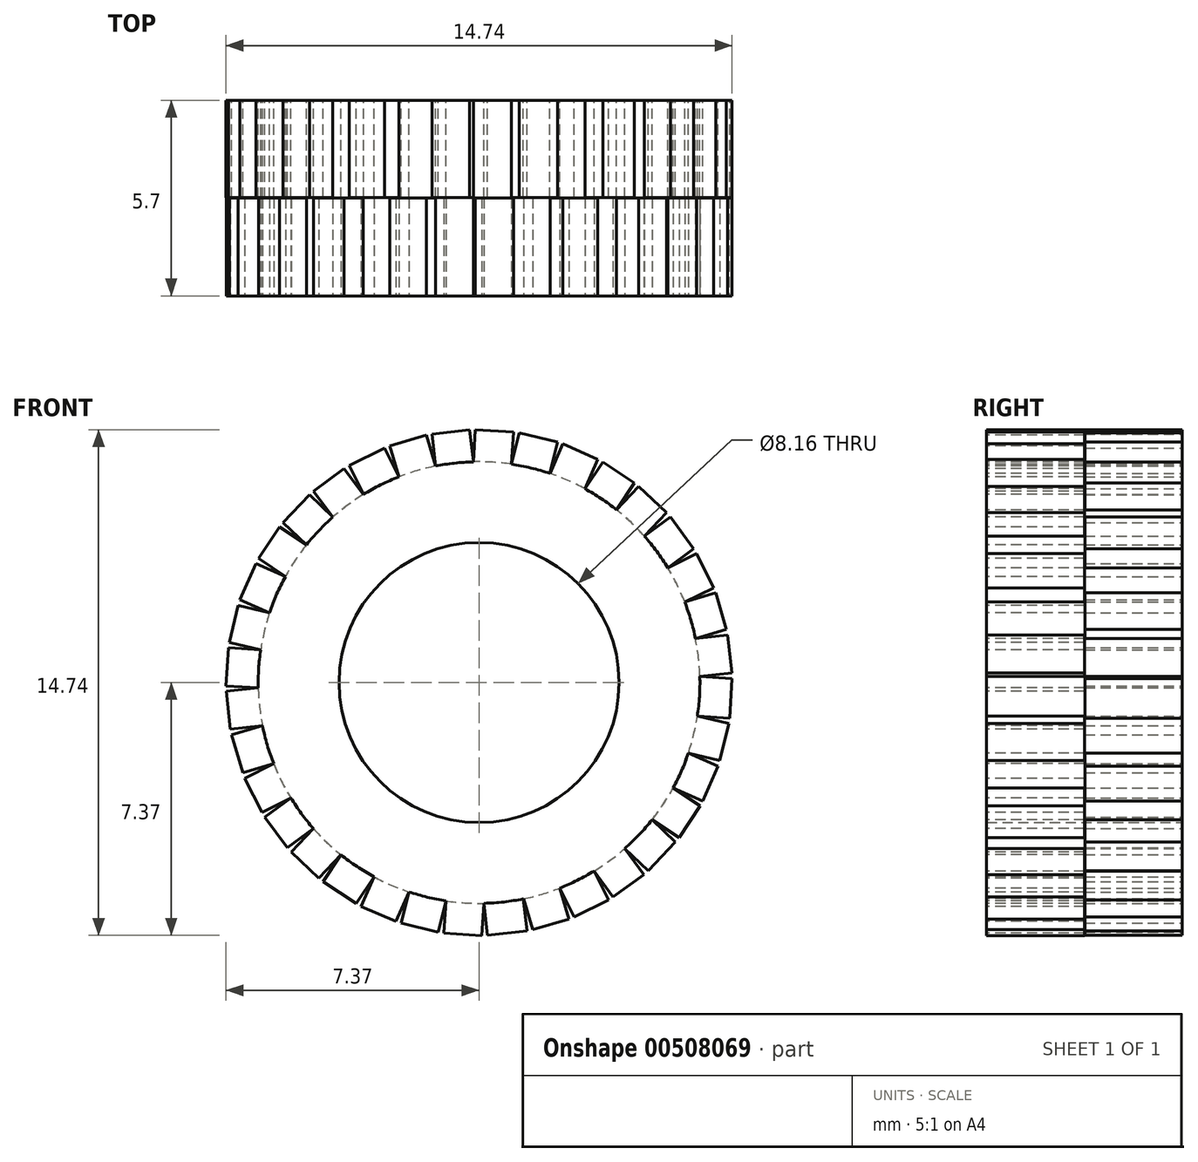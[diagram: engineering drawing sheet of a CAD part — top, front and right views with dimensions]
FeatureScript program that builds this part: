
annotation { "Feature Type Name" : "Feature", "Feature Type Description" : "" }
export const myFeature = defineFeature(function(context is Context, id is Id, definition is map)
    precondition{}
    {
        {
            var Q0;
            Q0=qCreatedBy(makeId("Front.planeOp"),FACE);
            var sketch = newSketch(context, id + "F0", { "sketchPlane" : qUnion([Q0])});
            skCircle(sketch, "E0", {"center": v(0, 0) * mm, "radius": 6.44 * mm});
            skCircle(sketch, "E1", {"center": v(0, 0) * mm, "radius": 4.08 * mm});
            skSolve(sketch);
        }
        {
            var Q0;
            Q0 = qSketchRegion(id + "F0", true);
            extrude(context, id + "F1", {"entities" : qUnion([Q0]), "depth" : 5.7 * mm, "offsetDistance" : 25 * mm});
        }
        {
            var Q0;
            Q0=makeQuery(id+"F1.opExtrude","CAP_FACE",FACE,{"disambiguationData":[OSD([sQuery(id+"F0.wireOp",EDGE,"E0"),sQuery(id+"F0.wireOp",EDGE,"E1")])],"isStart":false});
            var sketch = newSketch(context, id + "F2", { "sketchPlane" : qUnion([Q0])});
            skLineSegment(sketch, "E2", {"start": v(-2.33, 6) * mm, "end": v(-1.27, 6.3) * mm});
            skPoint(sketch, "E3.startSnap0", {"position": v(-1.8, 6.15) * mm});
            skLineSegment(sketch, "E4", {"start": v(-1.27, 6.3) * mm, "end": v(-1.53, 7.21) * mm});
            skLineSegment(sketch, "E5", {"start": v(-2.33, 6) * mm, "end": v(-2.6, 6.9) * mm});
            skLineSegment(sketch, "E6", {"start": v(-2.6, 6.9) * mm, "end": v(-1.53, 7.21) * mm});
            skLineSegment(sketch, "E7", {"start": v(-1.27, 6.3) * mm, "end": v(-0.17, 6.43) * mm});
            skLineSegment(sketch, "E8", {"start": v(-0.17, 6.43) * mm, "end": v(-0.1, 7.37) * mm});
            skLineSegment(sketch, "E9", {"start": v(-0.17, 6.43) * mm, "end": v(0.94, 6.37) * mm});
            skLineSegment(sketch, "E10", {"start": v(0.94, 6.37) * mm, "end": v(1, 7.3) * mm});
            skLineSegment(sketch, "E11", {"start": v(-0.1, 7.37) * mm, "end": v(1, 7.3) * mm});
            skLineSegment(sketch, "E12.1.0", {"start": v(-4.26, 4.82) * mm, "end": v(-4.82, 5.58) * mm});
            skLineSegment(sketch, "E12.1.1", {"start": v(-4.82, 5.58) * mm, "end": v(-3.93, 6.24) * mm});
            skLineSegment(sketch, "E12.1.2", {"start": v(-4.26, 4.82) * mm, "end": v(-3.37, 5.48) * mm});
            skLineSegment(sketch, "E12.1.3", {"start": v(-3.37, 5.48) * mm, "end": v(-3.93, 6.24) * mm});
            skLineSegment(sketch, "E12.1.4", {"start": v(-5.03, 4.02) * mm, "end": v(-4.26, 4.82) * mm});
            skLineSegment(sketch, "E12.1.5", {"start": v(-5.64, 3.1) * mm, "end": v(-5.03, 4.02) * mm});
            skLineSegment(sketch, "E12.1.6", {"start": v(-5.03, 4.02) * mm, "end": v(-5.8, 4.54) * mm});
            skLineSegment(sketch, "E12.1.7", {"start": v(-6.42, 3.61) * mm, "end": v(-5.8, 4.54) * mm});
            skLineSegment(sketch, "E12.1.8", {"start": v(-5.64, 3.1) * mm, "end": v(-6.42, 3.61) * mm});
            skLineSegment(sketch, "E12.2.0", {"start": v(-6.36, 0.95) * mm, "end": v(-7.28, 1.17) * mm});
            skLineSegment(sketch, "E12.2.1", {"start": v(-7.28, 1.17) * mm, "end": v(-7.02, 2.25) * mm});
            skLineSegment(sketch, "E12.2.2", {"start": v(-6.36, 0.95) * mm, "end": v(-6.1, 2.03) * mm});
            skLineSegment(sketch, "E12.2.3", {"start": v(-6.1, 2.03) * mm, "end": v(-7.02, 2.25) * mm});
            skLineSegment(sketch, "E12.2.4", {"start": v(-6.43, -0.15) * mm, "end": v(-6.36, 0.95) * mm});
            skLineSegment(sketch, "E12.2.5", {"start": v(-6.31, -1.26) * mm, "end": v(-6.43, -0.15) * mm});
            skLineSegment(sketch, "E12.2.6", {"start": v(-6.43, -0.15) * mm, "end": v(-7.37, -0.26) * mm});
            skLineSegment(sketch, "E12.2.7", {"start": v(-7.25, -1.36) * mm, "end": v(-7.37, -0.26) * mm});
            skLineSegment(sketch, "E12.2.8", {"start": v(-6.31, -1.26) * mm, "end": v(-7.25, -1.36) * mm});
            skPoint(sketch, "E12.center", {"position": v(0, 0) * mm});
            skLineSegment(sketch, "E13.1.3.0", {"start": v(-5.49, -3.36) * mm, "end": v(-6.33, -3.78) * mm});
            skLineSegment(sketch, "E13.3.3.0", {"start": v(-6.33, -3.78) * mm, "end": v(-6.82, -2.79) * mm});
            skLineSegment(sketch, "E13.6.3.0", {"start": v(-5.49, -3.36) * mm, "end": v(-5.98, -2.37) * mm});
            skLineSegment(sketch, "E13.9.3.0", {"start": v(-5.98, -2.37) * mm, "end": v(-6.82, -2.79) * mm});
            skLineSegment(sketch, "E13.12.3.0", {"start": v(-4.83, -4.25) * mm, "end": v(-5.49, -3.36) * mm});
            skLineSegment(sketch, "E13.15.3.0", {"start": v(-4.03, -5.02) * mm, "end": v(-4.83, -4.25) * mm});
            skLineSegment(sketch, "E13.18.3.0", {"start": v(-4.83, -4.25) * mm, "end": v(-5.48, -4.93) * mm});
            skLineSegment(sketch, "E13.21.3.0", {"start": v(-4.68, -5.7) * mm, "end": v(-5.48, -4.93) * mm});
            skLineSegment(sketch, "E13.24.3.0", {"start": v(-4.03, -5.02) * mm, "end": v(-4.68, -5.7) * mm});
            skLineSegment(sketch, "E13.1.4.0", {"start": v(-2.04, -6.1) * mm, "end": v(-2.42, -6.96) * mm});
            skLineSegment(sketch, "E13.3.4.0", {"start": v(-2.42, -6.96) * mm, "end": v(-3.44, -6.52) * mm});
            skLineSegment(sketch, "E13.6.4.0", {"start": v(-2.04, -6.1) * mm, "end": v(-3.06, -5.66) * mm});
            skLineSegment(sketch, "E13.9.4.0", {"start": v(-3.06, -5.66) * mm, "end": v(-3.44, -6.52) * mm});
            skLineSegment(sketch, "E13.12.4.0", {"start": v(-0.97, -6.36) * mm, "end": v(-2.04, -6.1) * mm});
            skLineSegment(sketch, "E13.15.4.0", {"start": v(0.14, -6.43) * mm, "end": v(-0.97, -6.36) * mm});
            skLineSegment(sketch, "E13.18.4.0", {"start": v(-0.97, -6.36) * mm, "end": v(-1.03, -7.3) * mm});
            skLineSegment(sketch, "E13.21.4.0", {"start": v(0.08, -7.37) * mm, "end": v(-1.03, -7.3) * mm});
            skLineSegment(sketch, "E13.24.4.0", {"start": v(0.14, -6.43) * mm, "end": v(0.08, -7.37) * mm});
            skLineSegment(sketch, "E13.1.5.0", {"start": v(2.36, -5.99) * mm, "end": v(2.62, -6.89) * mm});
            skLineSegment(sketch, "E13.3.5.0", {"start": v(2.62, -6.89) * mm, "end": v(1.56, -7.2) * mm});
            skLineSegment(sketch, "E13.6.5.0", {"start": v(2.36, -5.99) * mm, "end": v(1.3, -6.3) * mm});
            skLineSegment(sketch, "E13.9.5.0", {"start": v(1.3, -6.3) * mm, "end": v(1.56, -7.2) * mm});
            skLineSegment(sketch, "E13.12.5.0", {"start": v(3.35, -5.5) * mm, "end": v(2.36, -5.99) * mm});
            skLineSegment(sketch, "E13.15.5.0", {"start": v(4.24, -4.84) * mm, "end": v(3.35, -5.5) * mm});
            skLineSegment(sketch, "E13.18.5.0", {"start": v(3.35, -5.5) * mm, "end": v(3.9, -6.25) * mm});
            skLineSegment(sketch, "E13.21.5.0", {"start": v(4.8, -5.6) * mm, "end": v(3.9, -6.25) * mm});
            skLineSegment(sketch, "E13.24.5.0", {"start": v(4.24, -4.84) * mm, "end": v(4.8, -5.6) * mm});
            skLineSegment(sketch, "E13.1.6.0", {"start": v(5.65, -3.07) * mm, "end": v(6.44, -3.6) * mm});
            skLineSegment(sketch, "E13.3.6.0", {"start": v(6.44, -3.6) * mm, "end": v(5.83, -4.52) * mm});
            skLineSegment(sketch, "E13.6.6.0", {"start": v(5.65, -3.07) * mm, "end": v(5.04, -4) * mm});
            skLineSegment(sketch, "E13.9.6.0", {"start": v(5.04, -4) * mm, "end": v(5.83, -4.52) * mm});
            skLineSegment(sketch, "E13.12.6.0", {"start": v(6.1, -2.06) * mm, "end": v(5.65, -3.07) * mm});
            skLineSegment(sketch, "E13.15.6.0", {"start": v(6.36, -0.98) * mm, "end": v(6.1, -2.06) * mm});
            skLineSegment(sketch, "E13.18.6.0", {"start": v(6.1, -2.06) * mm, "end": v(7.01, -2.28) * mm});
            skLineSegment(sketch, "E13.21.6.0", {"start": v(7.27, -1.2) * mm, "end": v(7.01, -2.28) * mm});
            skLineSegment(sketch, "E13.24.6.0", {"start": v(6.36, -0.98) * mm, "end": v(7.27, -1.2) * mm});
            skLineSegment(sketch, "E13.1.7.0", {"start": v(6.3, 1.28) * mm, "end": v(7.24, 1.39) * mm});
            skLineSegment(sketch, "E13.3.7.0", {"start": v(7.24, 1.39) * mm, "end": v(7.37, 0.28) * mm});
            skLineSegment(sketch, "E13.6.7.0", {"start": v(6.3, 1.28) * mm, "end": v(6.43, 0.18) * mm});
            skLineSegment(sketch, "E13.9.7.0", {"start": v(6.43, 0.18) * mm, "end": v(7.37, 0.28) * mm});
            skLineSegment(sketch, "E13.12.7.0", {"start": v(6, 2.35) * mm, "end": v(6.3, 1.28) * mm});
            skLineSegment(sketch, "E13.15.7.0", {"start": v(5.5, 3.34) * mm, "end": v(6, 2.35) * mm});
            skLineSegment(sketch, "E13.18.7.0", {"start": v(6, 2.35) * mm, "end": v(6.83, 2.76) * mm});
            skLineSegment(sketch, "E13.21.7.0", {"start": v(6.34, 3.76) * mm, "end": v(6.83, 2.76) * mm});
            skLineSegment(sketch, "E13.24.7.0", {"start": v(5.5, 3.34) * mm, "end": v(6.34, 3.76) * mm});
            skLineSegment(sketch, "E13.1.8.0", {"start": v(4, 5.03) * mm, "end": v(4.65, 5.72) * mm});
            skLineSegment(sketch, "E13.3.8.0", {"start": v(4.65, 5.72) * mm, "end": v(5.46, 4.95) * mm});
            skLineSegment(sketch, "E13.6.8.0", {"start": v(4, 5.03) * mm, "end": v(4.81, 4.27) * mm});
            skLineSegment(sketch, "E13.9.8.0", {"start": v(4.81, 4.27) * mm, "end": v(5.46, 4.95) * mm});
            skLineSegment(sketch, "E13.12.8.0", {"start": v(3.08, 5.65) * mm, "end": v(4, 5.03) * mm});
            skLineSegment(sketch, "E13.15.8.0", {"start": v(2.07, 6.1) * mm, "end": v(3.08, 5.65) * mm});
            skLineSegment(sketch, "E13.18.8.0", {"start": v(3.08, 5.65) * mm, "end": v(3.46, 6.5) * mm});
            skLineSegment(sketch, "E13.21.8.0", {"start": v(2.44, 6.96) * mm, "end": v(3.46, 6.5) * mm});
            skLineSegment(sketch, "E13.24.8.0", {"start": v(2.07, 6.1) * mm, "end": v(2.44, 6.96) * mm});
            skSolve(sketch);
        }
        {
            var Q0;
            Q0 = qSketchRegion(id + "F2", true);
            extrude(context, id + "F3", {"entities" : qUnion([Q0]), "operationType" : NewBodyOperationType.ADD, "oppositeDirection" : true, "depth" : 2.85 * mm, "offsetDistance" : 25 * mm});
        }
        {
            var Q0;
            Q0=makeQuery(id+"F1.opExtrude","CAP_FACE",FACE,{"disambiguationData":[OSD([sQuery(id+"F0.wireOp",EDGE,"E0"),sQuery(id+"F0.wireOp",EDGE,"E1")])],"isStart":true});
            var sketch = newSketch(context, id + "F4", { "sketchPlane" : qUnion([Q0])});
            skLineSegment(sketch, "E14", {"start": v(-2.07, 6.1) * mm, "end": v(-0.95, 6.37) * mm});
            skLineSegment(sketch, "E15", {"start": v(-0.95, 6.37) * mm, "end": v(-1.17, 7.28) * mm});
            skLineSegment(sketch, "E16", {"start": v(-2.07, 6.1) * mm, "end": v(-2.29, 7) * mm});
            skLineSegment(sketch, "E17", {"start": v(-2.29, 7) * mm, "end": v(-1.17, 7.28) * mm});
            skLineSegment(sketch, "E18", {"start": v(-0.95, 6.37) * mm, "end": v(0.17, 6.43) * mm});
            skLineSegment(sketch, "E19", {"start": v(0.17, 6.43) * mm, "end": v(1.27, 6.3) * mm});
            skLineSegment(sketch, "E20", {"start": v(0.17, 6.43) * mm, "end": v(0.27, 7.37) * mm});
            skLineSegment(sketch, "E21", {"start": v(1.27, 6.3) * mm, "end": v(1.37, 7.24) * mm});
            skLineSegment(sketch, "E22", {"start": v(0.27, 7.37) * mm, "end": v(1.37, 7.24) * mm});
            skLineSegment(sketch, "E23.1.0", {"start": v(-5.5, 3.34) * mm, "end": v(-6.26, 3.9) * mm});
            skLineSegment(sketch, "E23.1.1", {"start": v(-6.26, 3.9) * mm, "end": v(-5.57, 4.83) * mm});
            skLineSegment(sketch, "E23.1.2", {"start": v(-5.5, 3.34) * mm, "end": v(-4.82, 4.27) * mm});
            skLineSegment(sketch, "E23.1.3", {"start": v(-4.82, 4.27) * mm, "end": v(-5.57, 4.83) * mm});
            skLineSegment(sketch, "E23.1.4", {"start": v(-4, 5.03) * mm, "end": v(-4.53, 5.82) * mm});
            skLineSegment(sketch, "E23.1.5", {"start": v(-4.53, 5.82) * mm, "end": v(-3.6, 6.43) * mm});
            skLineSegment(sketch, "E23.1.6", {"start": v(-3.08, 5.65) * mm, "end": v(-3.6, 6.43) * mm});
            skLineSegment(sketch, "E23.1.7", {"start": v(-4, 5.03) * mm, "end": v(-3.08, 5.65) * mm});
            skLineSegment(sketch, "E23.2.0", {"start": v(-6.36, -0.98) * mm, "end": v(-7.3, -1.03) * mm});
            skLineSegment(sketch, "E23.2.1", {"start": v(-7.3, -1.03) * mm, "end": v(-7.37, 0.12) * mm});
            skLineSegment(sketch, "E23.2.2", {"start": v(-6.36, -0.98) * mm, "end": v(-6.43, 0.17) * mm});
            skLineSegment(sketch, "E23.2.3", {"start": v(-6.43, 0.17) * mm, "end": v(-7.37, 0.12) * mm});
            skLineSegment(sketch, "E23.2.4", {"start": v(-6.3, 1.28) * mm, "end": v(-7.2, 1.55) * mm});
            skLineSegment(sketch, "E23.2.5", {"start": v(-7.2, 1.55) * mm, "end": v(-6.9, 2.61) * mm});
            skLineSegment(sketch, "E23.2.6", {"start": v(-6, 2.35) * mm, "end": v(-6.9, 2.61) * mm});
            skLineSegment(sketch, "E23.2.7", {"start": v(-6.3, 1.28) * mm, "end": v(-6, 2.35) * mm});
            skLineSegment(sketch, "E23.3.0", {"start": v(-4.25, -4.84) * mm, "end": v(-4.93, -5.48) * mm});
            skLineSegment(sketch, "E23.3.1", {"start": v(-4.93, -5.48) * mm, "end": v(-5.72, -4.65) * mm});
            skLineSegment(sketch, "E23.3.2", {"start": v(-4.25, -4.84) * mm, "end": v(-5.04, -4) * mm});
            skLineSegment(sketch, "E23.3.3", {"start": v(-5.04, -4) * mm, "end": v(-5.72, -4.65) * mm});
            skLineSegment(sketch, "E23.3.4", {"start": v(-5.65, -3.07) * mm, "end": v(-6.52, -3.45) * mm});
            skLineSegment(sketch, "E23.3.5", {"start": v(-6.52, -3.45) * mm, "end": v(-6.96, -2.43) * mm});
            skLineSegment(sketch, "E23.3.6", {"start": v(-6.1, -2.06) * mm, "end": v(-6.96, -2.43) * mm});
            skLineSegment(sketch, "E23.3.7", {"start": v(-5.65, -3.07) * mm, "end": v(-6.1, -2.06) * mm});
            skLineSegment(sketch, "E23.4.0", {"start": v(-0.14, -6.43) * mm, "end": v(-0.25, -7.37) * mm});
            skLineSegment(sketch, "E23.4.1", {"start": v(-0.25, -7.37) * mm, "end": v(-1.4, -7.24) * mm});
            skLineSegment(sketch, "E23.4.2", {"start": v(-0.14, -6.43) * mm, "end": v(-1.29, -6.3) * mm});
            skLineSegment(sketch, "E23.4.3", {"start": v(-1.29, -6.3) * mm, "end": v(-1.4, -7.24) * mm});
            skLineSegment(sketch, "E23.4.4", {"start": v(-2.36, -5.99) * mm, "end": v(-2.77, -6.83) * mm});
            skLineSegment(sketch, "E23.4.5", {"start": v(-2.77, -6.83) * mm, "end": v(-3.77, -6.34) * mm});
            skLineSegment(sketch, "E23.4.6", {"start": v(-3.35, -5.5) * mm, "end": v(-3.77, -6.34) * mm});
            skLineSegment(sketch, "E23.4.7", {"start": v(-2.36, -5.99) * mm, "end": v(-3.35, -5.5) * mm});
            skLineSegment(sketch, "E23.5.0", {"start": v(4.03, -5.02) * mm, "end": v(4.55, -5.8) * mm});
            skLineSegment(sketch, "E23.5.1", {"start": v(4.55, -5.8) * mm, "end": v(3.59, -6.44) * mm});
            skLineSegment(sketch, "E23.5.2", {"start": v(4.03, -5.02) * mm, "end": v(3.07, -5.66) * mm});
            skLineSegment(sketch, "E23.5.3", {"start": v(3.07, -5.66) * mm, "end": v(3.59, -6.44) * mm});
            skLineSegment(sketch, "E23.5.4", {"start": v(2.04, -6.1) * mm, "end": v(2.27, -7.02) * mm});
            skLineSegment(sketch, "E23.5.5", {"start": v(2.27, -7.02) * mm, "end": v(1.19, -7.28) * mm});
            skLineSegment(sketch, "E23.5.6", {"start": v(0.97, -6.36) * mm, "end": v(1.19, -7.28) * mm});
            skLineSegment(sketch, "E23.5.7", {"start": v(2.04, -6.1) * mm, "end": v(0.97, -6.36) * mm});
            skLineSegment(sketch, "E23.6.0", {"start": v(6.31, -1.26) * mm, "end": v(7.21, -1.52) * mm});
            skLineSegment(sketch, "E23.6.1", {"start": v(7.21, -1.52) * mm, "end": v(6.89, -2.63) * mm});
            skLineSegment(sketch, "E23.6.2", {"start": v(6.31, -1.26) * mm, "end": v(5.98, -2.36) * mm});
            skLineSegment(sketch, "E23.6.3", {"start": v(5.98, -2.36) * mm, "end": v(6.89, -2.63) * mm});
            skLineSegment(sketch, "E23.6.4", {"start": v(5.49, -3.36) * mm, "end": v(6.24, -3.92) * mm});
            skLineSegment(sketch, "E23.6.5", {"start": v(6.24, -3.92) * mm, "end": v(5.59, -4.81) * mm});
            skLineSegment(sketch, "E23.6.6", {"start": v(4.83, -4.25) * mm, "end": v(5.59, -4.81) * mm});
            skLineSegment(sketch, "E23.6.7", {"start": v(5.49, -3.36) * mm, "end": v(4.83, -4.25) * mm});
            skLineSegment(sketch, "E23.7.0", {"start": v(5.64, 3.1) * mm, "end": v(6.5, 3.47) * mm});
            skLineSegment(sketch, "E23.7.1", {"start": v(6.5, 3.47) * mm, "end": v(6.97, 2.41) * mm});
            skLineSegment(sketch, "E23.7.2", {"start": v(5.64, 3.1) * mm, "end": v(6.1, 2.04) * mm});
            skLineSegment(sketch, "E23.7.3", {"start": v(6.1, 2.04) * mm, "end": v(6.97, 2.41) * mm});
            skLineSegment(sketch, "E23.7.4", {"start": v(6.36, 0.95) * mm, "end": v(7.3, 1.01) * mm});
            skLineSegment(sketch, "E23.7.5", {"start": v(7.3, 1.01) * mm, "end": v(7.37, -0.1) * mm});
            skLineSegment(sketch, "E23.7.6", {"start": v(6.43, -0.15) * mm, "end": v(7.37, -0.1) * mm});
            skLineSegment(sketch, "E23.7.7", {"start": v(6.36, 0.95) * mm, "end": v(6.43, -0.15) * mm});
            skLineSegment(sketch, "E23.8.0", {"start": v(2.34, 6) * mm, "end": v(2.75, 6.84) * mm});
            skLineSegment(sketch, "E23.8.1", {"start": v(2.75, 6.84) * mm, "end": v(3.79, 6.33) * mm});
            skLineSegment(sketch, "E23.8.2", {"start": v(2.34, 6) * mm, "end": v(3.37, 5.48) * mm});
            skLineSegment(sketch, "E23.8.3", {"start": v(3.37, 5.48) * mm, "end": v(3.79, 6.33) * mm});
            skLineSegment(sketch, "E23.8.4", {"start": v(4.26, 4.82) * mm, "end": v(4.94, 5.47) * mm});
            skLineSegment(sketch, "E23.8.5", {"start": v(4.94, 5.47) * mm, "end": v(5.7, 4.67) * mm});
            skLineSegment(sketch, "E23.8.6", {"start": v(5.03, 4.02) * mm, "end": v(5.7, 4.67) * mm});
            skLineSegment(sketch, "E23.8.7", {"start": v(4.26, 4.82) * mm, "end": v(5.03, 4.02) * mm});
            skPoint(sketch, "E23.center", {"position": v(0, 0) * mm});
            skSolve(sketch);
        }
        {
            var Q0;
            Q0 = qSketchRegion(id + "F4", true);
            extrude(context, id + "F5", {"entities" : qUnion([Q0]), "operationType" : NewBodyOperationType.ADD, "oppositeDirection" : true, "depth" : 2.84 * mm, "offsetDistance" : 25 * mm});
        }
    });
